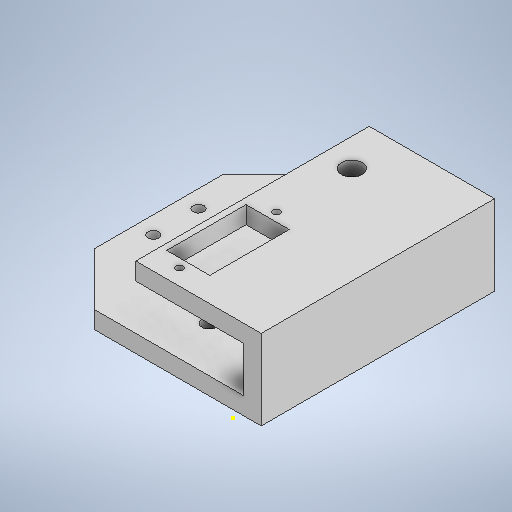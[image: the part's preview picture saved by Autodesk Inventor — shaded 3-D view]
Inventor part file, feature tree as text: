
AUTODESK INVENTOR PART (.ipt)
format: ipt  version: 2025.1 (Build 291241020, 241B)  size: 502,272 bytes
history: native  units: in
note: dims shown in document units (in); Inventor stores cm internally (conversion verified against a paired STEP export)
features: sketch x26, extrude x25
ambient origin geometry x8: Origin, YZ Plane, XZ Plane, XY Plane, X Axis, Y Axis, Z Axis, Center Point
bodies: Solid2 (feature_tree), Solid1 (feature_tree)
feature tree (51):
  extrude  "Extrusion1"  Depth=0.3937in
  extrude  "Extrusion2"  Depth=0.3937in TaperAngle=0.0deg
  extrude  "Extrusion3"  Depth=0.3937in TaperAngle=0.0deg
  extrude  "Extrusion4"  Depth=0.1181in
  extrude  "Extrusion5"  Depth=0.3937in TaperAngle=0.0deg
  extrude  "Extrusion6"  Depth=0.7087in
  extrude  "Extrusion7"  Depth=0.748in
  extrude  "Extrusion8"  Depth=2.3937in TaperAngle=0.0deg
  extrude  "Extrusion9"  Depth=0.3937in TaperAngle=0.0deg
  extrude  "Extrusion10"  TaperAngle=90.0deg  [1 undecoded]
  extrude  "Extrusion11"  Depth=0.5906in
  extrude  "Extrusion12"  Depth=0.3937in TaperAngle=0.0deg
  extrude  "Extrusion13"  Depth=0.1969in
  extrude  "Extrusion14"  Depth=0.1969in
  extrude  "Extrusion15"  Depth=1.0651in
  extrude  "Extrusion16"  Depth=0.122in
  extrude  "Extrusion17"  Depth=0.3937in TaperAngle=0.0deg
  sketch  "Sketch18"  dims[d48=0.3937in d49=0.0in d50=0.3937in d51=0.0in]
  extrude  "Extrusion18"  Depth=0.3937in TaperAngle=0.0deg
  extrude  "Extrusion19"  Depth=0.0787in
  extrude  "Extrusion20"  Depth=2.7313in TaperAngle=0.0deg
  extrude  "Extrusion21"  Depth=0.3937in
  extrude  "Extrusion22"  Depth=0.3937in
  extrude  "Extrusion23"  Depth=0.5906in
  extrude  "Extrusion24"  Depth=0.3937in TaperAngle=0.0deg
  extrude  "Extrusion25"  Depth=0.0787in TaperAngle=0.0deg
  sketch  "Sketch1"  dims[d0=0.3937in d1=0.0in d2=1.0945in]
  sketch  "Sketch2"  dims[d3=0.0787in d4=0.3937in d5=0.0in]
  sketch  "Sketch3"  dims[d6=0.0984in d7=0.3937in d8=0.0in]
  sketch  "Sketch4"  dims[d9=0.2362in d10=0.1181in]
  sketch  "Sketch5"  dims[d11=0.3937in d12=0.0in d13=2.3937in d14=0.0in]
  sketch  "Sketch6"  dims[d15=2.3937in d16=0.0in d17=0.7087in]
  sketch  "Sketch7"  dims[d18=0.1575in d19=0.748in]
  sketch  "Sketch8"  dims[d20=0.122in d21=2.3937in d22=0.0in]
  sketch  "Sketch9"  dims[d23=2.3937in d24=0.0in d25=0.3937in d26=0.0in]
  sketch  "Sketch10"  dims[d27=0.5118in d28=90.0deg]
  sketch  "Sketch11"  dims[d29=6.7687in d30=0.0in d31=0.5906in]
  sketch  "Sketch12"  dims[d32=6.7687in d33=0.0in d34=0.3937in d35=0.0in]
  sketch  "Sketch13"  dims[d36=0.3937in d37=0.1969in]
  sketch  "Sketch14"  dims[d38=0.3937in d39=0.0in d40=0.1969in]
  sketch  "Sketch15"  dims[d41=90.0deg d42=1.0651in]
  sketch  "Sketch16"  dims[d43=1.0651in d44=0.122in]
  sketch  "Sketch17"  dims[d45=0.122in d46=0.3937in d47=0.0in]
  sketch  "Sketch19"  dims[d52=0.3937in d53=0.0in d54=0.0787in]
  sketch  "Sketch20"  dims[d55=2.7313in d56=0.0in d57=2.7313in d58=0.0in]
  sketch  "Sketch21"  dims[d59=0.3937in d60=0.0in d61=0.2362in]
  sketch  "Sketch22"  dims[d62=0.3937in d63=0.0in d64=0.5906in]
  sketch  "Sketch23"  dims[d65=0.5906in d66=0.5906in]
  sketch  "Sketch24"  dims[d67=0.5906in d68=0.3937in d69=0.0in]
  sketch  "Sketch25"  dims[d70=0.1142in d71=0.0in d72=0.0787in d73=0.0in]
  sketch  "Sketch26"  dims[d74=0.0787in d75=0.0in]
note: 1 required parameter value undecoded (feature->parameter linkage not recoverable at this tier; creation-order binding heuristic only, values carry confidence <= 0.55)
